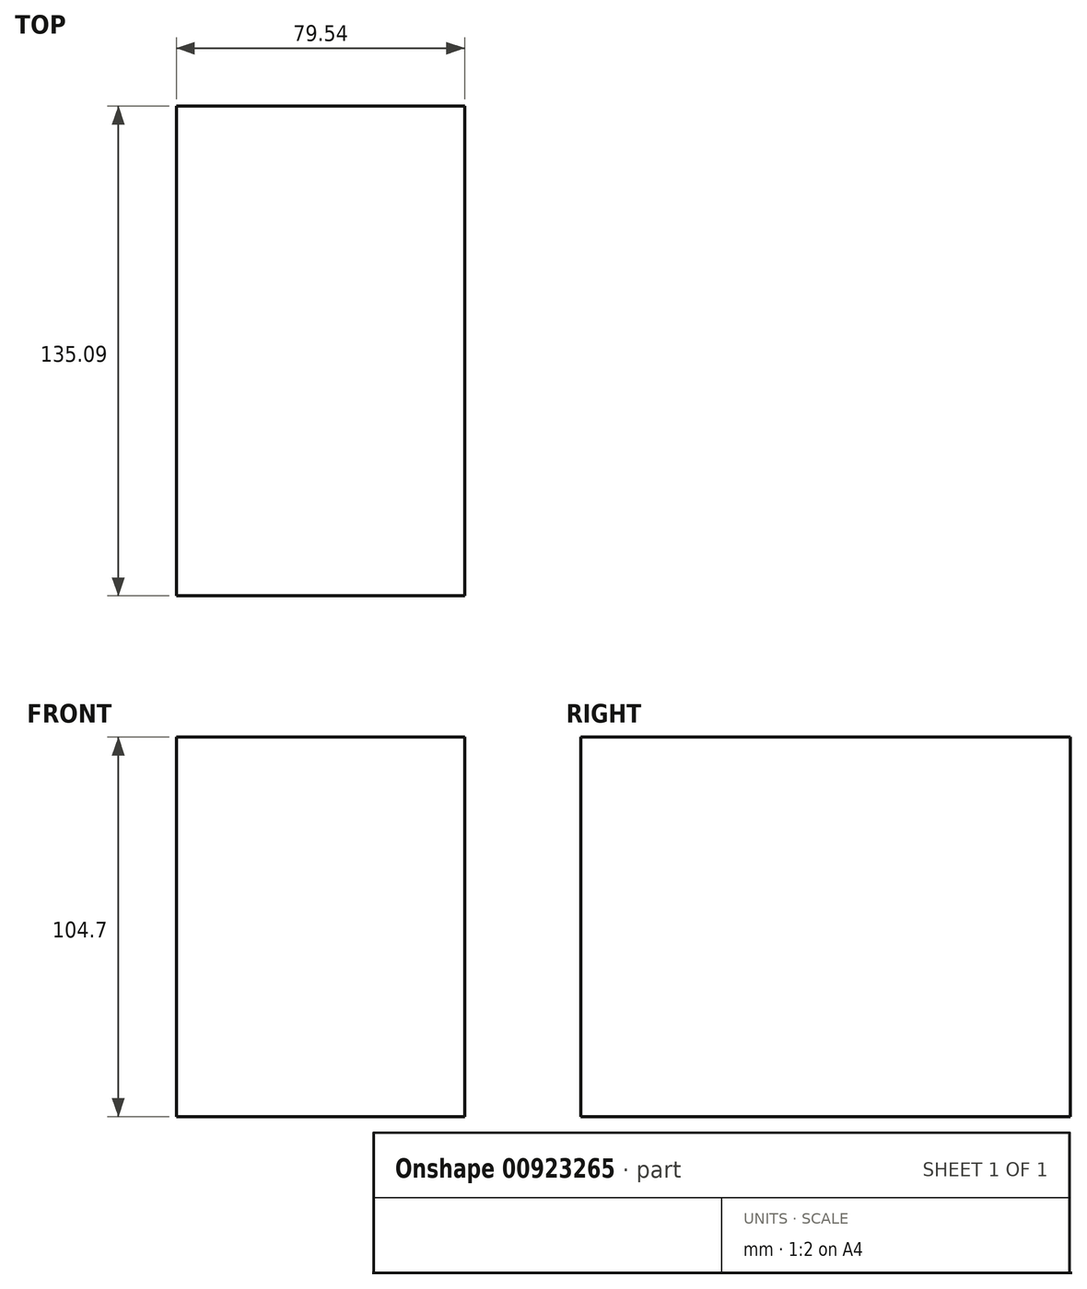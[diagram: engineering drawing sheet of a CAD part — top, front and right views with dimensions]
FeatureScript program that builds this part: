
annotation { "Feature Type Name" : "Feature", "Feature Type Description" : "" }
export const myFeature = defineFeature(function(context is Context, id is Id, definition is map)
    precondition{}
    {
        {
            var Q0;
            Q0=qCreatedBy(makeId("Right.planeOp"),FACE);
            var sketch = newSketch(context, id + "F0", { "sketchPlane" : qUnion([Q0])});
            skLineSegment(sketch, "E0.bottom", {"start": v(-168.08, 126.14) * mm, "end": v(-32.99, 126.14) * mm});
            skLineSegment(sketch, "E0.top", {"start": v(-168.08, 21.44) * mm, "end": v(-32.99, 21.44) * mm});
            skLineSegment(sketch, "E0.left", {"start": v(-168.08, 126.14) * mm, "end": v(-168.08, 21.44) * mm});
            skLineSegment(sketch, "E0.right", {"start": v(-32.99, 126.14) * mm, "end": v(-32.99, 21.44) * mm});
            skSolve(sketch);
        }
        {
            var Q0;
            Q0=makeQuery(id+"F0.imprint","IMPRINT",FACE,{"disambiguationData":[TD([[makeQuery(id+"F0.imprint","IMPRINT",EDGE,{"derivedFrom":sQuery(id+"F0.wireOp",EDGE,"E0.bottom")}),-1.0]])]});
            var Q1;
            Q1=sQuery(id+"F0.wireOp",EDGE,"E0.bottom");
            extrude(context, id + "F1", {"entities" : qUnion([Q0]), "surfaceEntities" : qUnion([Q1]), "endBound" : BoundingType.SYMMETRIC, "depth" : 79.53 * mm, "offsetDistance" : 25.4 * mm});
        }
    });
